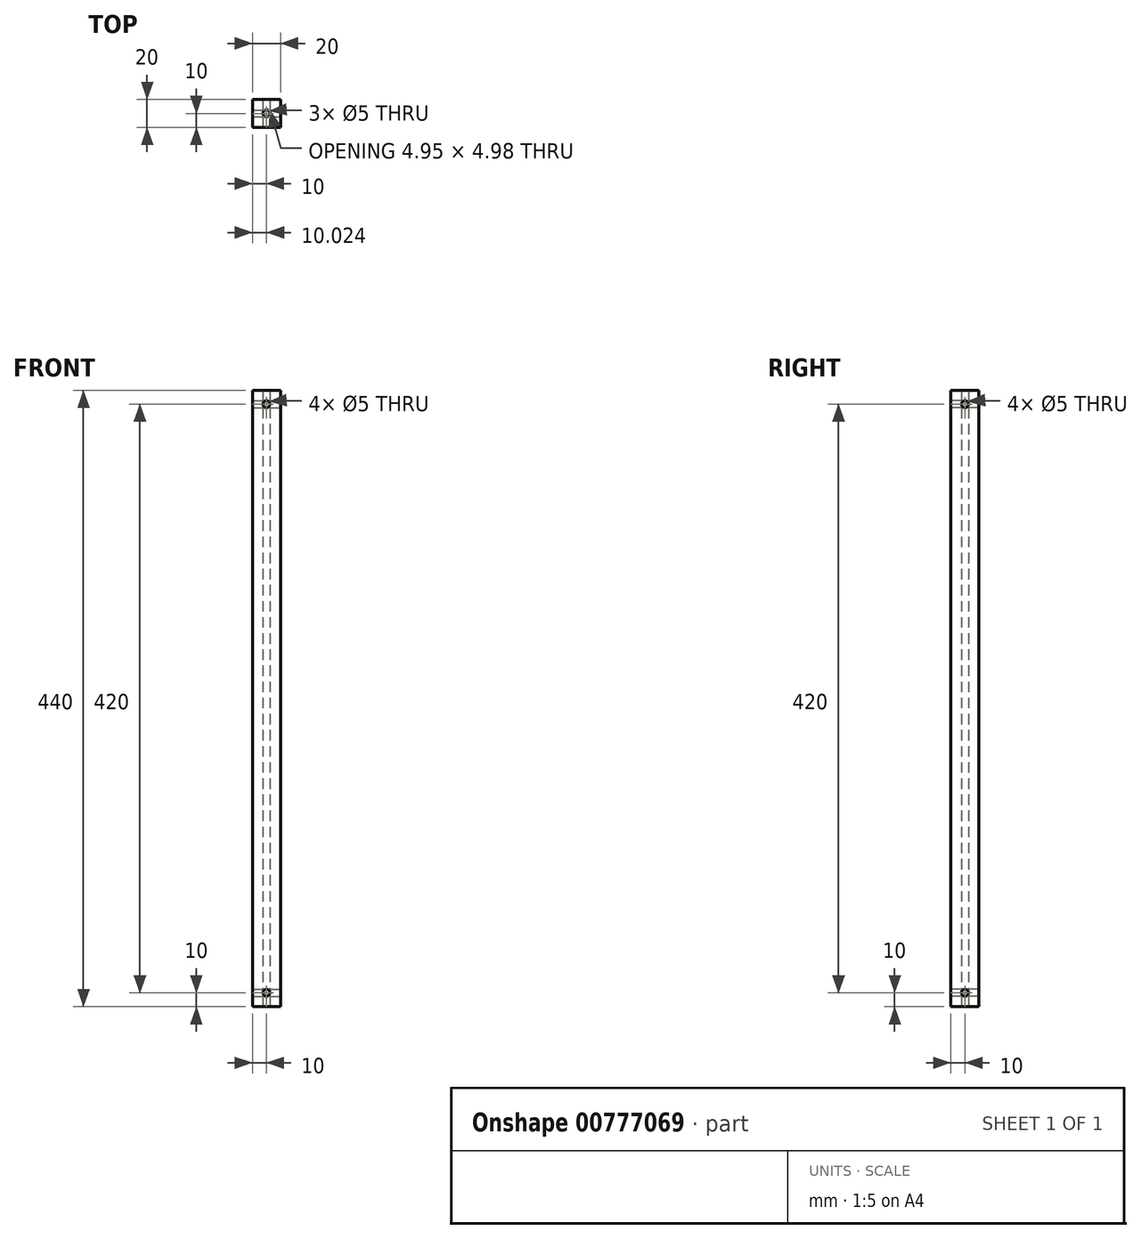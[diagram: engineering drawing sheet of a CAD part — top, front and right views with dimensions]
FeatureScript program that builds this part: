
annotation { "Feature Type Name" : "Feature", "Feature Type Description" : "" }
export const myFeature = defineFeature(function(context is Context, id is Id, definition is map)
    precondition{}
    {
        {
            var Q0;
            Q0=qCreatedBy(makeId("Top.planeOp"),FACE);
            var sketch = newSketch(context, id + "F0", { "sketchPlane" : qUnion([Q0])});
            skLineSegment(sketch, "E0.bottom", {"start": v(-10, 10) * mm, "end": v(10, 10) * mm});
            skLineSegment(sketch, "E0.top", {"start": v(-10, -10) * mm, "end": v(10, -10) * mm});
            skLineSegment(sketch, "E0.left", {"start": v(-10, 10) * mm, "end": v(-10, -10) * mm});
            skLineSegment(sketch, "E0.right", {"start": v(10, 10) * mm, "end": v(10, -10) * mm});
            skCircle(sketch, "E1", {"center": v(0, 0) * mm, "radius": 2.5 * mm});
            skSolve(sketch);
        }
        {
            var Q0;
            Q0=qSketchRegion(id+"F0",true);
            extrude(context, id + "F1", {"entities" : qUnion([Q0]), "depth" : 440 * mm, "offsetDistance" : 25 * mm});
        }
        {
            var Q0;
            Q0=makeQuery(id+"F1.opExtrude","SWEPT_FACE",FACE,{"disambiguationData":[OSD([sQuery(id+"F0.wireOp",EDGE,"E0.right")])]});
            var sketch = newSketch(context, id + "F2", { "sketchPlane" : qUnion([Q0])});
            skCircle(sketch, "E2", {"center": v(0, 10) * mm, "radius": 2.5 * mm});
            skCircle(sketch, "E3", {"center": v(0, 430) * mm, "radius": 2.5 * mm});
            skSolve(sketch);
        }
        {
            var Q0;
            Q0=qSketchRegion(id+"F2",true);
            extrude(context, id + "F3", {"entities" : qUnion([Q0]), "operationType" : NewBodyOperationType.REMOVE, "endBound" : BoundingType.THROUGH_ALL, "oppositeDirection" : true, "depth" : 25 * mm});
        }
        {
            var Q0;
            Q0=makeQuery(id+"F1.opExtrude","SWEPT_FACE",FACE,{"disambiguationData":[OSD([sQuery(id+"F0.wireOp",EDGE,"E0.top")])]});
            var sketch = newSketch(context, id + "F4", { "sketchPlane" : qUnion([Q0])});
            skCircle(sketch, "E4", {"center": v(0, 430) * mm, "radius": 2.5 * mm});
            skCircle(sketch, "E5", {"center": v(0, 10) * mm, "radius": 2.5 * mm});
            skSolve(sketch);
        }
        {
            var Q0;
            Q0=qSketchRegion(id+"F4",true);
            extrude(context, id + "F5", {"entities" : qUnion([Q0]), "operationType" : NewBodyOperationType.REMOVE, "endBound" : BoundingType.THROUGH_ALL, "oppositeDirection" : true, "depth" : 25 * mm});
        }
    });
